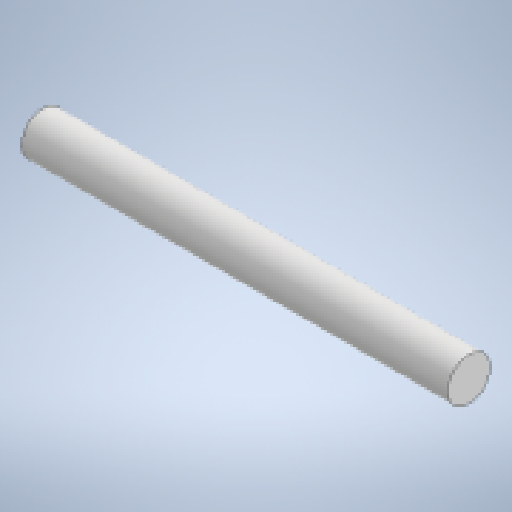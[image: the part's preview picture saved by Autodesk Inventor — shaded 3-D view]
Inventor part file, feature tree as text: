
AUTODESK INVENTOR PART (.ipt)
format: ipt  version: 2025.2 (Build 292293000, 293)  size: 119,296 bytes
history: native  units: in
note: dims shown in document units (in); Inventor stores cm internally (conversion verified against a paired STEP export)
features: extrude x1, sketch x1
ambient origin geometry x8: Origin, YZ Plane, XZ Plane, XY Plane, X Axis, Y Axis, Z Axis, Center Point
bodies: Solid1 (feature_tree)
feature tree (2):
  extrude  "Extrusion1"  Depth=2.5in TaperAngle=0.0deg
  sketch  "Sketch1"  dims[d0=0.25in d1=2.5in d2=0.0in]
